# Revit family: Data_Device-Network-Leviton-Cat_6-Plug
name_source: partatom
category: Data Devices
units: mm (PartAtom-declared; Revit-internal decimal feet)

## family parameters
Cut with Voids When Loaded = No
Host = Face
Maintain Annotation Orientation = Yes
OmniClass Number = 23.85.50.17
OmniClass Title = Communication and Data Processing Equipment
Part Type = Normal
Room Calculation Point = No
Round Connector Dimension = Use Diameter
Shared = Yes

## types (1)
- Cat 6 Plug RJ45
    Adapter Material = Plastic - Leviton - Orange
    Assembly Code = D5030600
    Date Last Modified = October 09, 2023
    Default Elevation = 24 "
    Description = Direct Attach Category 6 RJ45 Plug, Unshielded.
    Equipment Abbreviation = DAP
    Family Version = 1.0.0
    Has ID Windows = No
    Manufacturer = Leviton
    Minimum Order Quantity = 0
    Model Disclaimer = http://www.leviton.com
    Part Description = Direct Attach Category 6 RJ45 Plug, Unshielded.
    Product Documentation Link = https://www.leviton.com
    Quantity per Package = 0
    Shielded = No
    URL = http://www.leviton.com
    z Leviton Type = 3

## geometry (parser evidence)
native form markers: Blend x4, Sweep x2
no freeform markers — native parametric forms only
